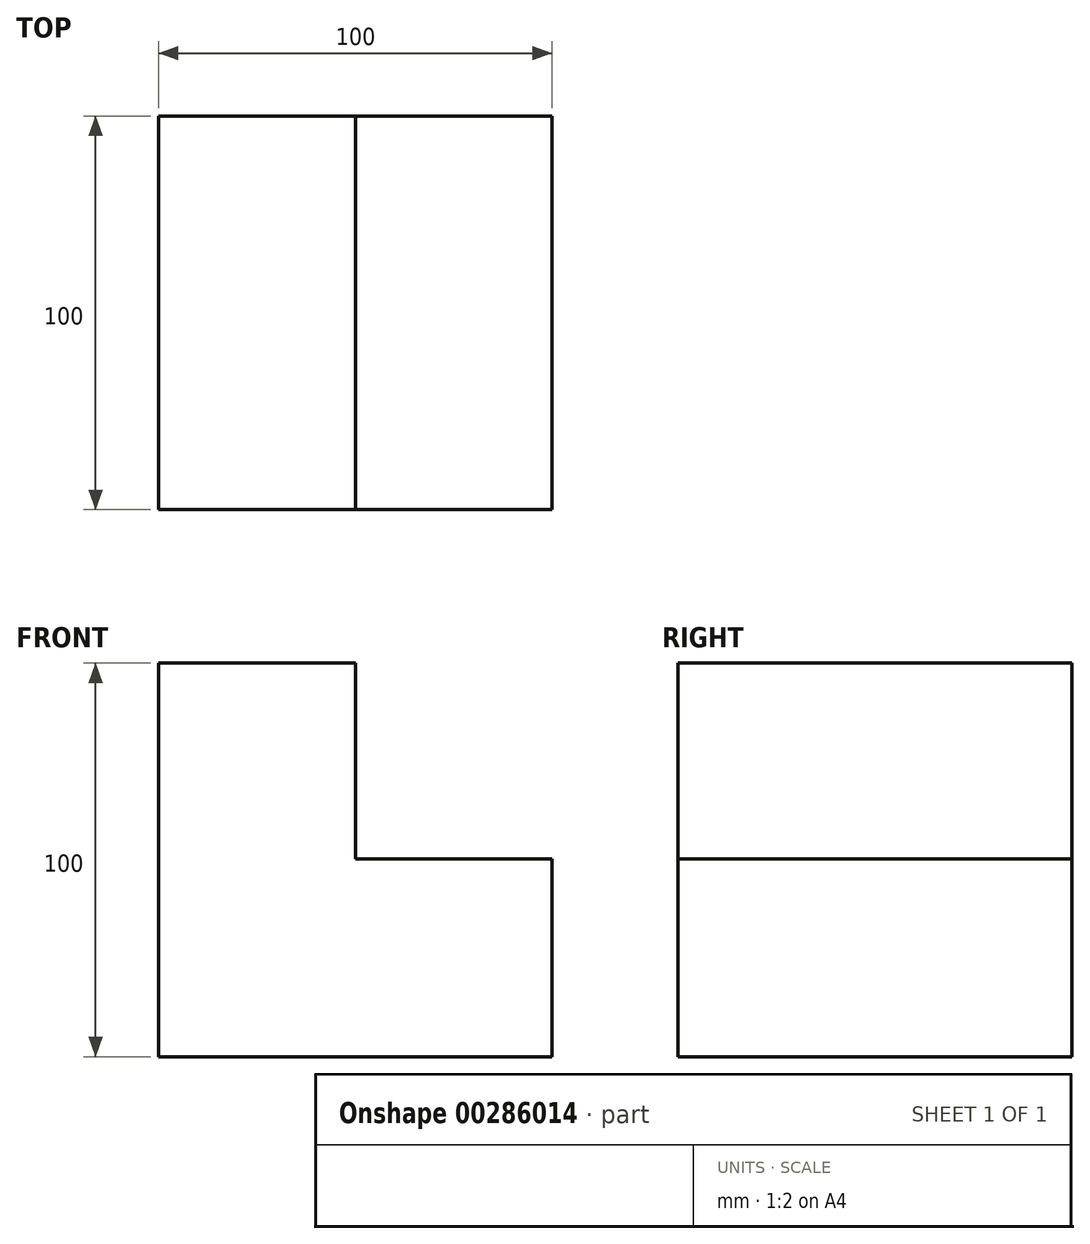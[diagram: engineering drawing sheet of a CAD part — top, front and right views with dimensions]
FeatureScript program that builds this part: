
annotation { "Feature Type Name" : "Feature", "Feature Type Description" : "" }
export const myFeature = defineFeature(function(context is Context, id is Id, definition is map)
    precondition{}
    {
        {
            var Q0;
            Q0=qCreatedBy(makeId("Front.planeOp"),FACE);
            var sketch = newSketch(context, id + "F0", { "sketchPlane" : qUnion([Q0])});
            skLineSegment(sketch, "E0.bottom", {"start": v(0, 115.32) * mm, "end": v(50, 115.32) * mm});
            skLineSegment(sketch, "E0.top", {"start": v(0, 15.32) * mm, "end": v(100, 15.32) * mm});
            skLineSegment(sketch, "E0.left", {"start": v(0, 115.32) * mm, "end": v(0, 15.32) * mm});
            skLineSegment(sketch, "E0.right", {"start": v(100, 65.53) * mm, "end": v(100, 15.32) * mm});
            skLineSegment(sketch, "E1.top", {"start": v(50, 65.53) * mm, "end": v(100, 65.53) * mm});
            skLineSegment(sketch, "E1.left", {"start": v(50, 115.53) * mm, "end": v(50, 65.53) * mm});
            skLineSegment(sketch, "E1.right", {"start": v(100, 115.53) * mm, "end": v(100, 115.32) * mm});
            skSolve(sketch);
        }
        {
            var Q0;
            {var subQ5=sQuery(id+"F0.wireOp",EDGE,"E1.bottom");Q0=makeQuery(id+"F0.imprint","IMPRINT",FACE,{"disambiguationData":[TD([[makeQuery(id+"F0.imprint","IMPRINT",EDGE,{"derivedFrom":subQ5}),-1.0]])]});}
            var Q1;
            Q1=makeQuery(id+"F0.imprint","IMPRINT",FACE,{"disambiguationData":[TD([[makeQuery(id+"F0.imprint","IMPRINT",EDGE,{"derivedFrom":sQuery(id+"F0.wireOp",EDGE,"E0.top")}),1.0]])]});
            extrude(context, id + "F1", {"entities" : qUnion([Q0, Q1]), "oppositeDirection" : true, "depth" : 100 * mm});
        }
    });
